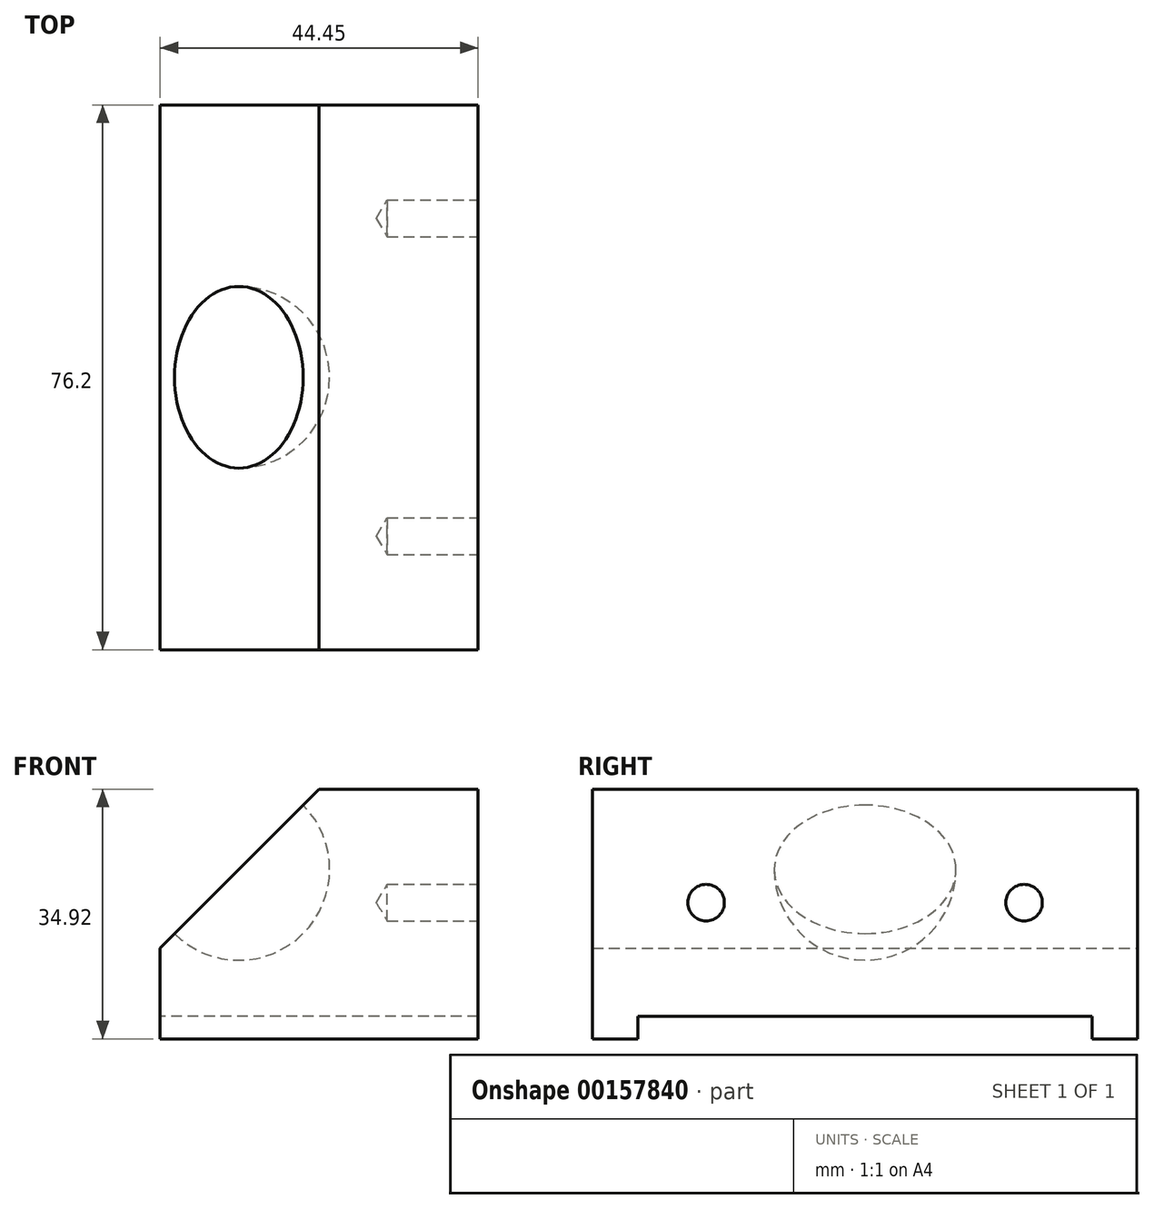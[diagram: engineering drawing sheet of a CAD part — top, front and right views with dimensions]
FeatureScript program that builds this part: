
annotation { "Feature Type Name" : "Feature", "Feature Type Description" : "" }
export const myFeature = defineFeature(function(context is Context, id is Id, definition is map)
    precondition{}
    {
        {
            var Q0;
            Q0=qCreatedBy(makeId("Front.planeOp"),FACE);
            var sketch = newSketch(context, id + "F0", { "sketchPlane" : qUnion([Q0])});
            skLineSegment(sketch, "E0", {"start": v(0, 0) * mm, "end": v(0, 12.7) * mm});
            skLineSegment(sketch, "E1", {"start": v(0, 12.7) * mm, "end": v(22.22, 34.93) * mm});
            skLineSegment(sketch, "E2", {"start": v(22.22, 34.93) * mm, "end": v(44.45, 34.93) * mm});
            skLineSegment(sketch, "E3", {"start": v(44.45, 34.93) * mm, "end": v(44.45, 0) * mm});
            skLineSegment(sketch, "E4", {"start": v(44.45, 0) * mm, "end": v(0, 0) * mm});
            skSolve(sketch);
        }
        {
            var Q0;
            Q0=makeQuery(id+"F0.imprint","IMPRINT",FACE,{"disambiguationData":[TD([[makeQuery(id+"F0.imprint","IMPRINT",EDGE,{"derivedFrom":sQuery(id+"F0.wireOp",EDGE,"E0")}),-1.0]])]});
            extrude(context, id + "F1", {"entities" : qUnion([Q0]), "endBound" : BoundingType.SYMMETRIC, "depth" : 76.2 * mm});
        }
        {
            var Q0;
            Q0=makeQuery(id+"F1.opExtrude","SWEPT_FACE",FACE,{"disambiguationData":[OSD([sQuery(id+"F0.wireOp",EDGE,"E0")])]});
            var sketch = newSketch(context, id + "F2", { "sketchPlane" : qUnion([Q0])});
            skLineSegment(sketch, "E5.bottom", {"start": v(-31.75, 0) * mm, "end": v(31.75, 0) * mm});
            skLineSegment(sketch, "E5.top", {"start": v(-31.75, 3.18) * mm, "end": v(31.75, 3.18) * mm});
            skLineSegment(sketch, "E5.left", {"start": v(-31.75, 0) * mm, "end": v(-31.75, 3.17) * mm});
            skLineSegment(sketch, "E5.right", {"start": v(31.75, 0) * mm, "end": v(31.75, 3.18) * mm});
            skSolve(sketch);
        }
        {
            var Q0;
            Q0=makeQuery(id+"F2.imprint","IMPRINT",FACE,{"disambiguationData":[TD([[makeQuery(id+"F2.imprint","IMPRINT",EDGE,{"derivedFrom":sQuery(id+"F2.wireOp",EDGE,"E5.bottom")}),-1.0]])]});
            extrude(context, id + "F3", {"entities" : qUnion([Q0]), "operationType" : NewBodyOperationType.REMOVE, "endBound" : BoundingType.THROUGH_ALL, "oppositeDirection" : true, "depth" : 25.4 * mm});
        }
        {
            var Q0;
            Q0=makeQuery(id+"F1.opExtrude","SWEPT_FACE",FACE,{"disambiguationData":[OSD([sQuery(id+"F0.wireOp",EDGE,"E3")])]});
            var sketch = newSketch(context, id + "F4", { "sketchPlane" : qUnion([Q0])});
            skLineSegment(sketch, "E6", {"start": v(-22.23, 19.05) * mm, "end": v(22.23, 19.05) * mm});
            skSolve(sketch);
        }
        {
            var Q0;
            Q0=sQuery(id+"F4.wireOp",VERTEX,"E6.start");
            var Q1;
            Q1=sQuery(id+"F4.wireOp",VERTEX,"E6.end");
            var Q2;
            Q2=makeQuery(id+"F1.opExtrude","SWEPT_BODY",BODY,{"disambiguationData":[OSD([sQuery(id+"F0.wireOp",EDGE,"E0"),sQuery(id+"F0.wireOp",EDGE,"E1"),sQuery(id+"F0.wireOp",EDGE,"E2"),sQuery(id+"F0.wireOp",EDGE,"E3"),sQuery(id+"F0.wireOp",EDGE,"E4")])]});
            hole(context, id + "F5", {"style" : HoleStyle.SIMPLE, "endStyle" : HoleEndStyle.BLIND, "standardTappedOrClearance" : lookupTablePath({ "standard" : "ANSI", "engagement" : "75%", "pitch" : "20 tpi", "size" : "1/4", "type" : "Tapped" }), "standardBlindInLast" : lookupTablePath({ "standard" : "ANSI", "engagement" : "75%", "pitch" : "20 tpi", "size" : "1/4", "type" : "Tapped" }), "holeDiameter" : 5.1 * mm, "holeDepth" : 12.7 * mm, "startFromSketch" : true, "locations" : qUnion([Q0, Q1]), "scope" : qUnion([Q2]), "majorDiameter" : 6.35 * mm});
        }
        {
            var Q0;
            Q0=makeQuery(id+"F1.opExtrude","SWEPT_FACE",FACE,{"disambiguationData":[OSD([sQuery(id+"F0.wireOp",EDGE,"E1")])]});
            var sketch = newSketch(context, id + "F6", { "sketchPlane" : qUnion([Q0])});
            skLineSegment(sketch, "E7", {"start": v(0, 17.28) * mm, "end": v(0, 31.8) * mm, "construction": true});
            skPoint(sketch, "E7.startSnap0", {"position": v(0, 8.98) * mm});
            skPoint(sketch, "E7.endSnap0", {"position": v(0, 40.41) * mm});
            skArc(sketch, "E8", {"start": v(0, 37.24) * mm, "mid": v(-12.7, 24.54) * mm, "end": v(0, 11.84) * mm});
            skLineSegment(sketch, "E9", {"start": v(0, 11.84) * mm, "end": v(0, 37.24) * mm});
            skSolve(sketch);
        }
        {
            var Q0;
            Q0 = qSketchRegion(id + "F6", true);
            var Q1;
            Q1=sQuery(id+"F6.wireOp",EDGE,"E9");
            revolve(context, id + "F7", {"operationType" : NewBodyOperationType.REMOVE, "surfaceOperationType" : NewSurfaceOperationType.NEW, "entities" : qUnion([Q0]), "axis" : qUnion([Q1]), "revolveType" : RevolveType.ONE_DIRECTION, "oppositeDirection" : true, "angle" : 180 * degree});
        }
    });
